# Revit family: Grohe_PlumbingFixture_Tempesta250_Cube_HeadShower_26685000a
name_source: partatom
category: Plumbing Fixtures
revit_build: Autodesk Revit 2018 (Build: 20190510_1515(x64)
units: mm (PartAtom-declared; Revit-internal decimal feet)

## family parameters
Cut with Voids When Loaded = No
Host = Face
OmniClass Number = 23.45.05.14.17
OmniClass Title = Showers
Part Type = Normal
Room Calculation Point = No
Round Connector Dimension = Use Diameter
Shared = No

## types (1)
- 26685000
    ADACompliant = No
    Assembly Code = D2010710
    AssetType = Fixed
    BIMObjectName = Grohe_PlumbingFixture_Tempesta250_Cube_HeadShower_26685000
    CWFU = 4.5
    ClassificationName = Uniclass 2015
    ClassificationValue = Pr_40_20_87_76
    ColdWaterConnectionDiameter = 10 mm  [stored 0.0328084 ft]
    Cost = 0 $
    Default Elevation = 0 mm  [stored 0 ft]
    Description = Head shower 1 spray. Rain. 250 mm x 250 mm. head shower with white rear cover. ball joint with turning angle ± 10°. connection thread ½". GROHE EcoJoy 9.5 l/min flow limiter. GROHE DreamSpray perfect spray pattern. GROHE StarLight chrome finish. SpeedClean anti-lime system. Inner WaterGuide for a longer life. suitable for instantaneous heater. min. recommended pressure 1.0 bar.
    DocumentationCertificates = www.bimstore.co
    DocumentationInstallationGuide = www.bimstore.co
    DocumentationLiterature = www.bimstore.co
    DocumentationMaintenance = www.bimstore.co
    DocumentationTechnical = www.bimstore.co
    DurationUnit = Years
    Ecojoy = Yes
    ExpectedLife = 0
    FaucetMaterial = Grohe-Chrome
    Features = Head shower 1 spray. Rain. 250 mm x 250 mm. head shower with white rear cover. ball joint with turning angle ± 10°. connection thread ½". GROHE EcoJoy 9.5 l/min flow limiter. GROHE DreamSpray perfect spray pattern. GROHE StarLight chrome finish. SpeedClean anti-lime system. Inner WaterGuide for a longer life. suitable for instantaneous heater. min. recommended pressure 1.0 bar.
    Finish = Chrome
    HWFU = 4.5
    HotWaterConnectionDiameter = 10 mm  [stored 0.0328084 ft]
    IfcExportAs = IfcPipeFitting
    IfcExportType = IfcPipeFittingType
    Keynote = N13
    LowEmittingMaterial = No
    Manufacturer = Grohe
    ManufacturerName = Grohe
    MasterformatNumber = 01 52 19
    MasterformatTitle = Sanitary Facilities
    Model = Tempesta 250 Cube
    ModelNumber = 26685000
    ModelReference = Tempesta 250 Cube
    NBSDescription = Shower heads
    NBSObjectName = Grohe - Shower heads
    NBSReference = 45-35-70/333
    NominalDepth = 0 mm  [stored 0 ft]
    NominalHeight = 0 mm  [stored 0 ft]
    NominalLength = 0 mm  [stored 0 ft]
    PipeMaterial = GroheLimited-Pipework
    ProductionYear = 2020
    Type Comments = 26685000
    TypeName = 26685000
    URL = www.grohe.com
    WarrantyDurationLabor = 0
    WarrantyDurationParts = 0
    WarrantyDurationUnit = Years
    _BSBibleVersion = 16
    _BimSpecGuid = 0
    _CurrentRevision = 1
    _DistributedBy = www.bimstore.co
    _ObjectUserGuide = www.bimstore.co

note: [stored X ft] marks values corroborated as IEEE doubles in the binary element streams (Revit-internal decimal feet)

## geometry (parser evidence)
native form markers: Sweep x2
no freeform markers — native parametric forms only
